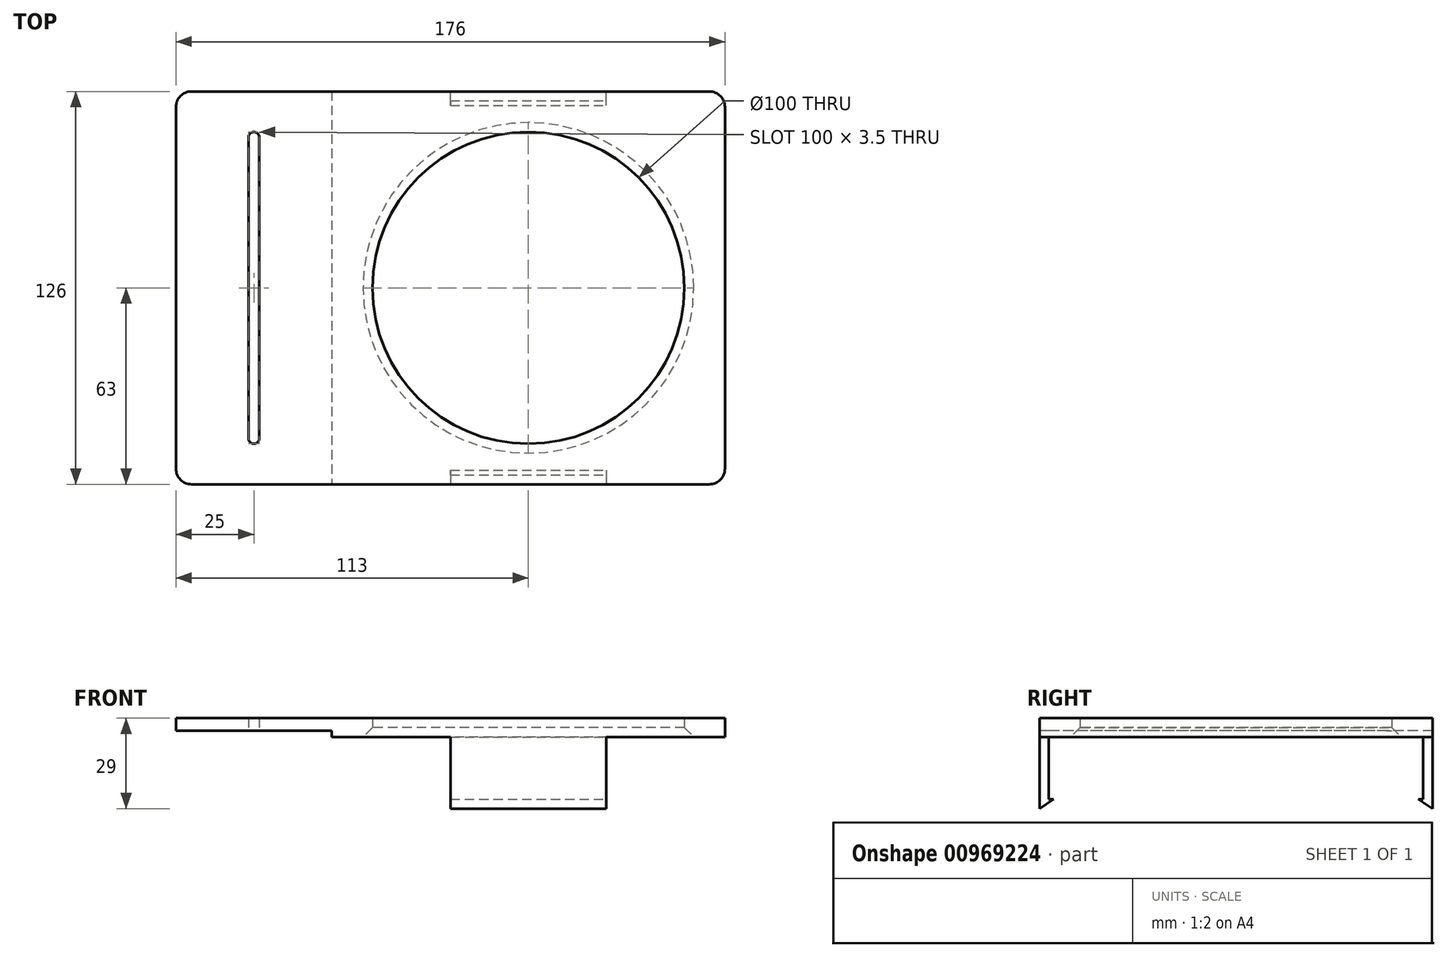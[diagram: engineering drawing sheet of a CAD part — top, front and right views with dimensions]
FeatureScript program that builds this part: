
annotation { "Feature Type Name" : "Feature", "Feature Type Description" : "" }
export const myFeature = defineFeature(function(context is Context, id is Id, definition is map)
    precondition{}
    {
        {
            var Q0;
            Q0=qCreatedBy(makeId("Top.planeOp"),FACE);
            var sketch = newSketch(context, id + "F0", { "sketchPlane" : qUnion([Q0])});
            skLineSegment(sketch, "E0.bottom", {"start": v(-60, 60) * mm, "end": v(60, 60) * mm});
            skLineSegment(sketch, "E0.top", {"start": v(-60, -60) * mm, "end": v(60, -60) * mm});
            skLineSegment(sketch, "E0.left", {"start": v(-60, 60) * mm, "end": v(-60, -60) * mm});
            skLineSegment(sketch, "E0.right", {"start": v(60, 60) * mm, "end": v(60, -60) * mm});
            skLineSegment(sketch, "E1.0", {"start": v(-63, 63) * mm, "end": v(-63, -63) * mm});
            skLineSegment(sketch, "E1.1", {"start": v(-63, 63) * mm, "end": v(63, 63) * mm});
            skLineSegment(sketch, "E1.2", {"start": v(63, 63) * mm, "end": v(63, -63) * mm});
            skLineSegment(sketch, "E1.3", {"start": v(-63, -63) * mm, "end": v(63, -63) * mm});
            skLineSegment(sketch, "E2.bottom", {"start": v(-63, 63) * mm, "end": v(-113, 63) * mm});
            skLineSegment(sketch, "E2.top", {"start": v(-63, -63) * mm, "end": v(-113, -63) * mm});
            skLineSegment(sketch, "E2.right", {"start": v(-113, 63) * mm, "end": v(-113, -63) * mm});
            skCircle(sketch, "E3", {"center": v(0, 0) * mm, "radius": 50 * mm});
            skLineSegment(sketch, "E4", {"start": v(0, 50) * mm, "end": v(-113, 50) * mm, "construction": true});
            skPoint(sketch, "E4.startSnap0", {"position": v(0, 60) * mm});
            skLineSegment(sketch, "E5", {"start": v(0, -50) * mm, "end": v(-113, -50) * mm, "construction": true});
            skPoint(sketch, "E5.startSnap0", {"position": v(0, -60) * mm});
            skLineSegment(sketch, "E6", {"start": v(-88, 63) * mm, "end": v(-88, -63) * mm, "construction": true});
            skCircle(sketch, "E7", {"center": v(-88, -48.25) * mm, "radius": 1.75 * mm});
            skCircle(sketch, "E8.MirrorC", {"center": v(-88, 48.25) * mm, "radius": 1.75 * mm});
            skLineSegment(sketch, "E9", {"start": v(-89.75, 48.25) * mm, "end": v(-89.75, -48.25) * mm});
            skLineSegment(sketch, "E10", {"start": v(-86.25, -48.25) * mm, "end": v(-86.25, 48.25) * mm});
            skSolve(sketch);
        }
        {
            var Q0;
            Q0=makeQuery(id+"F0.imprint","IMPRINT",FACE,{"disambiguationData":[TD([[makeQuery(id+"F0.imprint","IMPRINT",EDGE,{"derivedFrom":sQuery(id+"F0.wireOp",EDGE,"E0.bottom")}),-1.0]])]});
            var Q1;
            Q1=makeQuery(id+"F0.imprint","IMPRINT",FACE,{"disambiguationData":[TD([[makeQuery(id+"F0.imprint","IMPRINT",EDGE,{"derivedFrom":sQuery(id+"F0.wireOp",EDGE,"E0.bottom")}),1.0]])]});
            var Q2;
            Q2=makeQuery(id+"F0.imprint","IMPRINT",FACE,{"disambiguationData":[TD([[makeQuery(id+"F0.imprint","IMPRINT",EDGE,{"derivedFrom":sQuery(id+"F0.wireOp",EDGE,"E2.bottom")}),1.0]])]});
            extrude(context, id + "F1", {"entities" : qUnion([Q0, Q1, Q2]), "depth" : 4 * mm, "offsetDistance" : 25 * mm});
        }
        {
            var Q0;
            Q0=makeQuery(id+"F0.imprint","IMPRINT",FACE,{"disambiguationData":[TD([[makeQuery(id+"F0.imprint","IMPRINT",EDGE,{"derivedFrom":sQuery(id+"F0.wireOp",EDGE,"E0.bottom")}),1.0]])]});
            var Q1;
            Q1=makeQuery(id+"F0.imprint","IMPRINT",FACE,{"disambiguationData":[TD([[makeQuery(id+"F0.imprint","IMPRINT",EDGE,{"derivedFrom":sQuery(id+"F0.wireOp",EDGE,"E0.bottom")}),-1.0]])]});
            extrude(context, id + "F2", {"entities" : qUnion([Q0, Q1]), "operationType" : NewBodyOperationType.ADD, "oppositeDirection" : true, "depth" : 2 * mm, "offsetDistance" : 25 * mm});
        }
        {
            var Q0;
            Q0=makeQuery(id+"F1.opExtrude","SWEPT_EDGE",EDGE,{"disambiguationData":[OSD([sQuery(id+"F0.wireOp",EDGE,"E2.bottom"),sQuery(id+"F0.wireOp",EDGE,"E2.right")])]});
            var Q1;
            Q1=makeQuery(id+"F1.opExtrude","SWEPT_EDGE",EDGE,{"disambiguationData":[OSD([sQuery(id+"F0.wireOp",EDGE,"E2.top"),sQuery(id+"F0.wireOp",EDGE,"E2.right")])]});
            var Q2;
            {var subQ0=sQuery(id+"F0.wireOp",EDGE,"E1.2");var subQ1=sQuery(id+"F0.wireOp",EDGE,"E1.1");Q2=makeQuery(id+"F2.boolean.opBoolean","MERGE",EDGE,{"derivedFrom":[makeQuery(id+"F1.opExtrude","SWEPT_EDGE",EDGE,{"disambiguationData":[OSD([subQ1,subQ0])]}),makeQuery(id+"F2.opExtrude","SWEPT_EDGE",EDGE,{"disambiguationData":[OSD([subQ1,subQ0])]})]});}
            var Q3;
            {var subQ0=sQuery(id+"F0.wireOp",EDGE,"E1.3");var subQ1=sQuery(id+"F0.wireOp",EDGE,"E1.2");Q3=makeQuery(id+"F2.boolean.opBoolean","MERGE",EDGE,{"derivedFrom":[makeQuery(id+"F1.opExtrude","SWEPT_EDGE",EDGE,{"disambiguationData":[OSD([subQ1,subQ0])]}),makeQuery(id+"F2.opExtrude","SWEPT_EDGE",EDGE,{"disambiguationData":[OSD([subQ1,subQ0])]})]});}
            fillet(context, id + "F3", {"entities" : qUnion([Q0, Q1, Q2, Q3]), "radius" : 5 * mm, "tangentPropagation" : true, "allowEdgeOverflow" : false});
        }
        {
            var Q0;
            Q0=makeQuery(id+"F2.opExtrude","CAP_FACE",FACE,{"disambiguationData":[OSD([sQuery(id+"F0.wireOp",EDGE,"E1.1"),sQuery(id+"F0.wireOp",EDGE,"E1.2"),sQuery(id+"F0.wireOp",EDGE,"E1.3"),sQuery(id+"F0.wireOp",EDGE,"E1.0"),sQuery(id+"F0.wireOp",EDGE,"E3")])],"isStart":false});
            var sketch = newSketch(context, id + "F4", { "sketchPlane" : qUnion([Q0])});
            skLineSegment(sketch, "E11.0", {"start": v(-60, 60) * mm, "end": v(60, 60) * mm});
            skLineSegment(sketch, "E12.0", {"start": v(-60, -60) * mm, "end": v(60, -60) * mm});
            skLineSegment(sketch, "E13", {"start": v(-25, -60) * mm, "end": v(-25, -63) * mm});
            skLineSegment(sketch, "E14.MirrorCS", {"start": v(25, -60) * mm, "end": v(25, -63) * mm});
            skLineSegment(sketch, "E15.MirrorCS", {"start": v(-25, 60) * mm, "end": v(-25, 63) * mm});
            skLineSegment(sketch, "E16.MirrorCS", {"start": v(25, 60) * mm, "end": v(25, 63) * mm});
            skSolve(sketch);
        }
        {
            var Q0;
            {var subQ0=sQuery(id+"F4.wireOp",EDGE,"E15.MirrorCS");Q0=makeQuery(id+"F4.imprint","IMPRINT",FACE,{"disambiguationData":[TD([[makeQuery(id+"F4.imprint","IMPRINT",EDGE,{"derivedFrom":subQ0}),-1.0]])]});}
            var Q1;
            {var subQ0=sQuery(id+"F4.wireOp",EDGE,"E13");Q1=makeQuery(id+"F4.imprint","IMPRINT",FACE,{"disambiguationData":[TD([[makeQuery(id+"F4.imprint","IMPRINT",EDGE,{"derivedFrom":subQ0}),1.0]])]});}
            extrude(context, id + "F5", {"entities" : qUnion([Q0, Q1]), "operationType" : NewBodyOperationType.ADD, "depth" : 20 * mm, "offsetDistance" : 25 * mm});
        }
        {
            var Q0;
            Q0=makeQuery(id+"F5.opExtrude","CAP_FACE",FACE,{"disambiguationData":[OSD([sQuery(id+"F0.wireOp",EDGE,"E1.1"),sQuery(id+"F4.wireOp",EDGE,"E12.0"),sQuery(id+"F4.wireOp",EDGE,"E13"),sQuery(id+"F4.wireOp",EDGE,"E14.MirrorCS")])],"isStart":false});
            var sketch = newSketch(context, id + "F6", { "sketchPlane" : qUnion([Q0])});
            skLineSegment(sketch, "E17", {"start": v(-25, -60) * mm, "end": v(-25, -58.5) * mm});
            skLineSegment(sketch, "E18", {"start": v(-25, -58.5) * mm, "end": v(25, -58.5) * mm});
            skLineSegment(sketch, "E19", {"start": v(25, -58.5) * mm, "end": v(25, -60) * mm});
            skLineSegment(sketch, "E20", {"start": v(-25, -60) * mm, "end": v(-25, -63) * mm});
            skLineSegment(sketch, "E21", {"start": v(-25, -63) * mm, "end": v(25, -63) * mm});
            skLineSegment(sketch, "E22", {"start": v(25, -63) * mm, "end": v(25, -60) * mm});
            skLineSegment(sketch, "E23.MirrorCS", {"start": v(-25, 58.5) * mm, "end": v(25, 58.5) * mm});
            skLineSegment(sketch, "E24.MirrorCS", {"start": v(-25, 60) * mm, "end": v(-25, 58.5) * mm});
            skLineSegment(sketch, "E25.MirrorCS", {"start": v(-25, 60) * mm, "end": v(-25, 63) * mm});
            skLineSegment(sketch, "E26.MirrorCS", {"start": v(-25, 63) * mm, "end": v(25, 63) * mm});
            skLineSegment(sketch, "E27.MirrorCS", {"start": v(25, 63) * mm, "end": v(25, 60) * mm});
            skLineSegment(sketch, "E28.MirrorCS", {"start": v(25, 58.5) * mm, "end": v(25, 60) * mm});
            skSolve(sketch);
        }
        {
            var Q0;
            Q0=makeQuery(id+"F6.imprint","IMPRINT",FACE,{"disambiguationData":[TD([[makeQuery(id+"F6.imprint","IMPRINT",EDGE,{"derivedFrom":sQuery(id+"F6.wireOp",EDGE,"E23.MirrorCS")}),1.0]])]});
            var Q1;
            Q1=makeQuery(id+"F6.imprint","IMPRINT",FACE,{"disambiguationData":[TD([[makeQuery(id+"F6.imprint","IMPRINT",EDGE,{"derivedFrom":sQuery(id+"F6.wireOp",EDGE,"E17")}),-1.0]])]});
            var Q2;
            Q2=makeQuery(id+"F6.imprint","IMPRINT",FACE,{"disambiguationData":[TD([[makeQuery(id+"F6.imprint","IMPRINT",EDGE,{"derivedFrom":sQuery(id+"F6.wireOp",EDGE,"E20")}),1.0]])]});
            extrude(context, id + "F7", {"entities" : qUnion([Q0, Q1, Q2]), "operationType" : NewBodyOperationType.ADD, "depth" : 3 * mm, "offsetDistance" : 25 * mm});
        }
        {
            var Q0;
            Q0=makeQuery(id+"F7.boolean.opBoolean","MERGE",FACE,{"derivedFrom":[makeQuery(id+"F5.opExtrude","SWEPT_FACE",FACE,{"disambiguationData":[OSD([sQuery(id+"F4.wireOp",EDGE,"E16.MirrorCS")])]}),makeQuery(id+"F7.opExtrude","SWEPT_FACE",FACE,{"disambiguationData":[OSD([sQuery(id+"F6.wireOp",EDGE,"E27.MirrorCS"),sQuery(id+"F6.wireOp",EDGE,"E28.MirrorCS")])]})]});
            var sketch = newSketch(context, id + "F8", { "sketchPlane" : qUnion([Q0])});
            skLineSegment(sketch, "E29", {"start": v(-58.5, -22) * mm, "end": v(-63, -25) * mm});
            skLineSegment(sketch, "E30", {"start": v(-63, -25) * mm, "end": v(-58.5, -25) * mm});
            skLineSegment(sketch, "E31", {"start": v(-58.5, -25) * mm, "end": v(-58.5, -22) * mm});
            skLineSegment(sketch, "E32.MirrorCS", {"start": v(58.5, -22) * mm, "end": v(63, -25) * mm});
            skLineSegment(sketch, "E33.MirrorCS", {"start": v(63, -25) * mm, "end": v(58.5, -25) * mm});
            skLineSegment(sketch, "E34.MirrorCS", {"start": v(58.5, -25) * mm, "end": v(58.5, -22) * mm});
            skSolve(sketch);
        }
        {
            var Q0;
            Q0=makeQuery(id+"F8.imprint","IMPRINT",FACE,{"disambiguationData":[TD([[makeQuery(id+"F8.imprint","IMPRINT",EDGE,{"derivedFrom":sQuery(id+"F8.wireOp",EDGE,"E29")}),1.0]])]});
            var Q1;
            Q1=makeQuery(id+"F8.imprint","IMPRINT",FACE,{"disambiguationData":[TD([[makeQuery(id+"F8.imprint","IMPRINT",EDGE,{"derivedFrom":sQuery(id+"F8.wireOp",EDGE,"E32.MirrorCS")}),-1.0]])]});
            var Q2;
            Q2=makeQuery(id+"F7.boolean.opBoolean","MERGE",FACE,{"derivedFrom":[makeQuery(id+"F5.opExtrude","SWEPT_FACE",FACE,{"disambiguationData":[OSD([sQuery(id+"F4.wireOp",EDGE,"E15.MirrorCS")])]}),makeQuery(id+"F7.opExtrude","SWEPT_FACE",FACE,{"disambiguationData":[OSD([sQuery(id+"F6.wireOp",EDGE,"E24.MirrorCS"),sQuery(id+"F6.wireOp",EDGE,"E25.MirrorCS")])]})]});
            extrude(context, id + "F9", {"entities" : qUnion([Q0, Q1]), "operationType" : NewBodyOperationType.REMOVE, "endBound" : BoundingType.UP_TO_SURFACE, "oppositeDirection" : true, "depth" : 25 * mm, "endBoundEntityFace" : qUnion([Q2]), "offsetDistance" : 25 * mm});
        }
        {
            var Q0;
            Q0=makeQuery(id+"F2.opExtrude","CAP_EDGE",EDGE,{"disambiguationData":[OSD([sQuery(id+"F0.wireOp",EDGE,"E3")])],"isStart":false});
            chamfer(context, id + "F10", {"entities" : qUnion([Q0]), "width" : 3 * mm, "tangentPropagation" : true});
        }
    });
